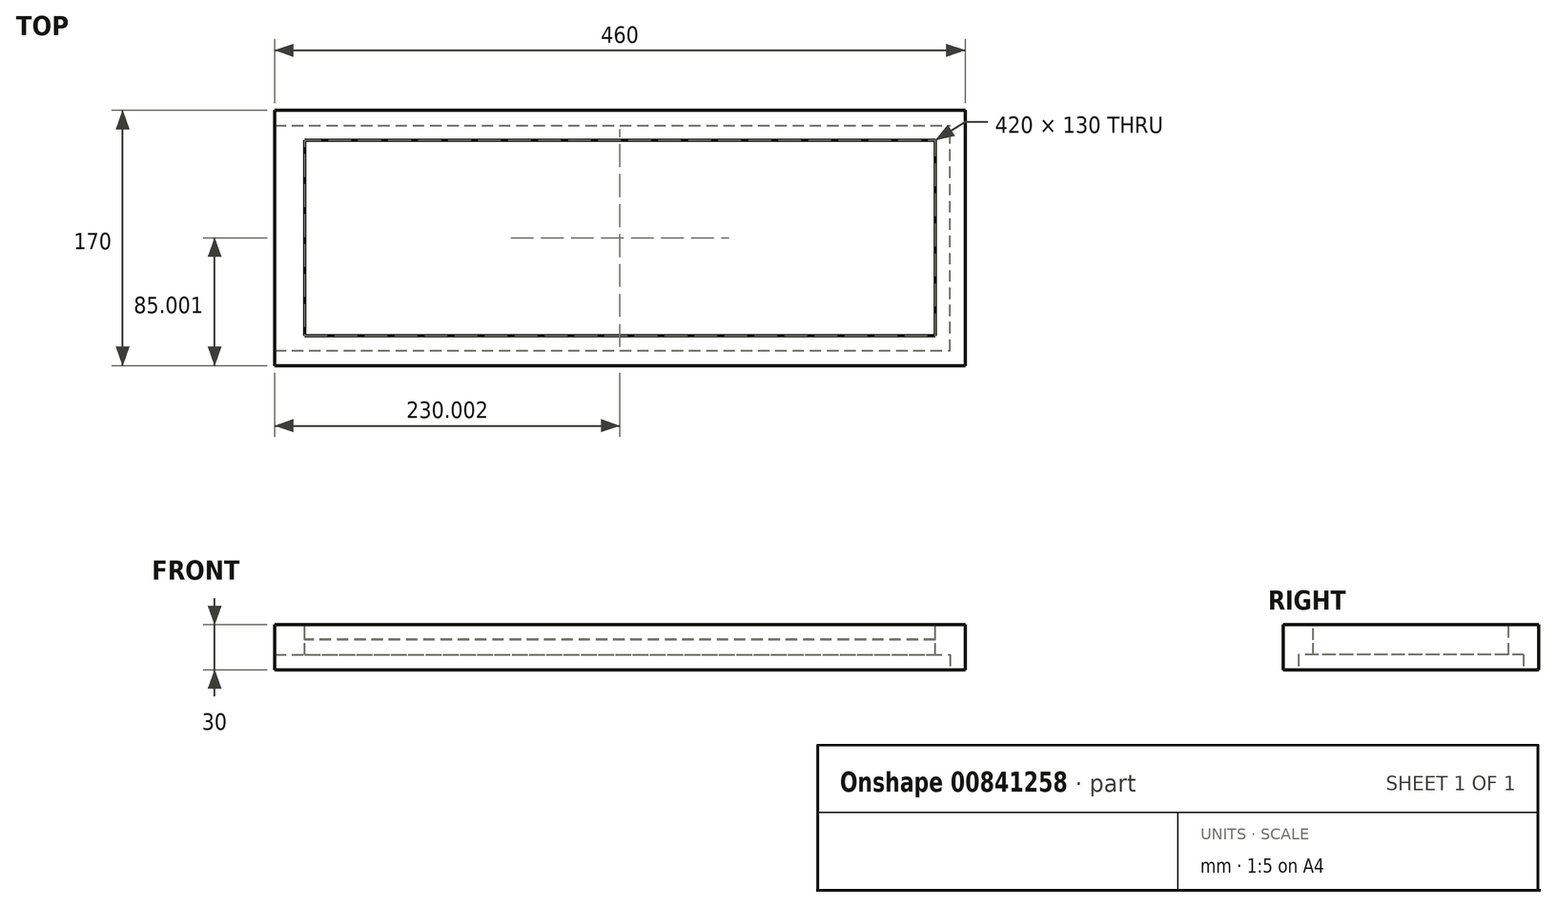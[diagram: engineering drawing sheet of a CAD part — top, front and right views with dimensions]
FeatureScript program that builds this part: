
annotation { "Feature Type Name" : "Feature", "Feature Type Description" : "" }
export const myFeature = defineFeature(function(context is Context, id is Id, definition is map)
    precondition{}
    {
        {
            var Q0;
            Q0=qCreatedBy(makeId("Top.planeOp"),FACE);
            var sketch = newSketch(context, id + "F0", { "sketchPlane" : qUnion([Q0])});
            skLineSegment(sketch, "E0.bottom", {"start": v(-188.85, 66.71) * mm, "end": v(271.15, 66.71) * mm});
            skLineSegment(sketch, "E0.top", {"start": v(-188.85, -103.29) * mm, "end": v(271.15, -103.29) * mm});
            skLineSegment(sketch, "E0.left", {"start": v(-188.85, 66.71) * mm, "end": v(-188.85, -103.29) * mm});
            skLineSegment(sketch, "E0.right", {"start": v(271.15, 66.71) * mm, "end": v(271.15, -103.29) * mm});
            skSolve(sketch);
        }
        {
            var Q0;
            Q0 = qSketchRegion(id + "F0", true);
            extrude(context, id + "F1", {"entities" : qUnion([Q0]), "depth" : 30 * mm, "offsetDistance" : 25 * mm});
        }
        {
            var Q0;
            Q0=makeQuery(id+"F1.opExtrude","CAP_FACE",FACE,{"disambiguationData":[OSD([sQuery(id+"F0.wireOp",EDGE,"E0.bottom"),sQuery(id+"F0.wireOp",EDGE,"E0.top"),sQuery(id+"F0.wireOp",EDGE,"E0.left"),sQuery(id+"F0.wireOp",EDGE,"E0.right")])],"isStart":false});
            var sketch = newSketch(context, id + "F2", { "sketchPlane" : qUnion([Q0])});
            skLineSegment(sketch, "E1.bottom", {"start": v(-168.85, 46.71) * mm, "end": v(251.15, 46.71) * mm});
            skLineSegment(sketch, "E1.top", {"start": v(-168.85, -83.29) * mm, "end": v(251.15, -83.29) * mm});
            skLineSegment(sketch, "E1.left", {"start": v(-168.85, 46.71) * mm, "end": v(-168.85, -83.29) * mm});
            skLineSegment(sketch, "E1.right", {"start": v(251.15, 46.71) * mm, "end": v(251.15, -83.29) * mm});
            skSolve(sketch);
        }
        {
            var Q0;
            Q0 = qSketchRegion(id + "F2", true);
            extrude(context, id + "F3", {"entities" : qUnion([Q0]), "operationType" : NewBodyOperationType.REMOVE, "endBound" : BoundingType.UP_TO_NEXT, "oppositeDirection" : true, "depth" : 25 * mm, "offsetDistance" : 25 * mm});
        }
        {
            var Q0;
            Q0=makeQuery(id+"F1.opExtrude","CAP_FACE",FACE,{"disambiguationData":[OSD([sQuery(id+"F0.wireOp",EDGE,"E0.bottom"),sQuery(id+"F0.wireOp",EDGE,"E0.top"),sQuery(id+"F0.wireOp",EDGE,"E0.left"),sQuery(id+"F0.wireOp",EDGE,"E0.right")])],"isStart":true});
            var sketch = newSketch(context, id + "F4", { "sketchPlane" : qUnion([Q0])});
            skLineSegment(sketch, "E2.bottom", {"start": v(-188.85, 93.29) * mm, "end": v(261.15, 93.29) * mm});
            skLineSegment(sketch, "E2.top", {"start": v(-188.85, -56.71) * mm, "end": v(261.15, -56.71) * mm});
            skLineSegment(sketch, "E2.left", {"start": v(-188.85, 93.29) * mm, "end": v(-188.85, -56.71) * mm});
            skLineSegment(sketch, "E2.right", {"start": v(261.15, 93.29) * mm, "end": v(261.15, -56.71) * mm});
            skSolve(sketch);
        }
        {
            var Q0;
            Q0 = qSketchRegion(id + "F4", true);
            extrude(context, id + "F5", {"entities" : qUnion([Q0]), "operationType" : NewBodyOperationType.REMOVE, "oppositeDirection" : true, "depth" : 10 * mm, "offsetDistance" : 25 * mm});
        }
        {
            var Q0;
            Q0=makeQuery(id+"F3.boolean.opBoolean","COPY",FACE,{"derivedFrom":makeQuery(id+"F3.opExtrude","SWEPT_FACE",FACE,{"disambiguationData":[OSD([sQuery(id+"F2.wireOp",EDGE,"E1.top")])]})});
            var sketch = newSketch(context, id + "F6", { "sketchPlane" : qUnion([Q0])});
            skLineSegment(sketch, "E3.bottom", {"start": v(-251.15, 20) * mm, "end": v(168.85, 20) * mm});
            skLineSegment(sketch, "E3.top", {"start": v(-251.15, 20.1) * mm, "end": v(168.85, 20.1) * mm});
            skLineSegment(sketch, "E3.left", {"start": v(-251.15, 20) * mm, "end": v(-251.15, 20.1) * mm});
            skLineSegment(sketch, "E3.right", {"start": v(168.85, 20) * mm, "end": v(168.85, 20.1) * mm});
            skSolve(sketch);
        }
        {
            var Q0;
            Q0 = qSketchRegion(id + "F6", true);
            extrude(context, id + "F7", {"entities" : qUnion([Q0]), "operationType" : NewBodyOperationType.REMOVE, "oppositeDirection" : true, "depth" : 0.1 * mm, "offsetDistance" : 25 * mm});
        }
    });
